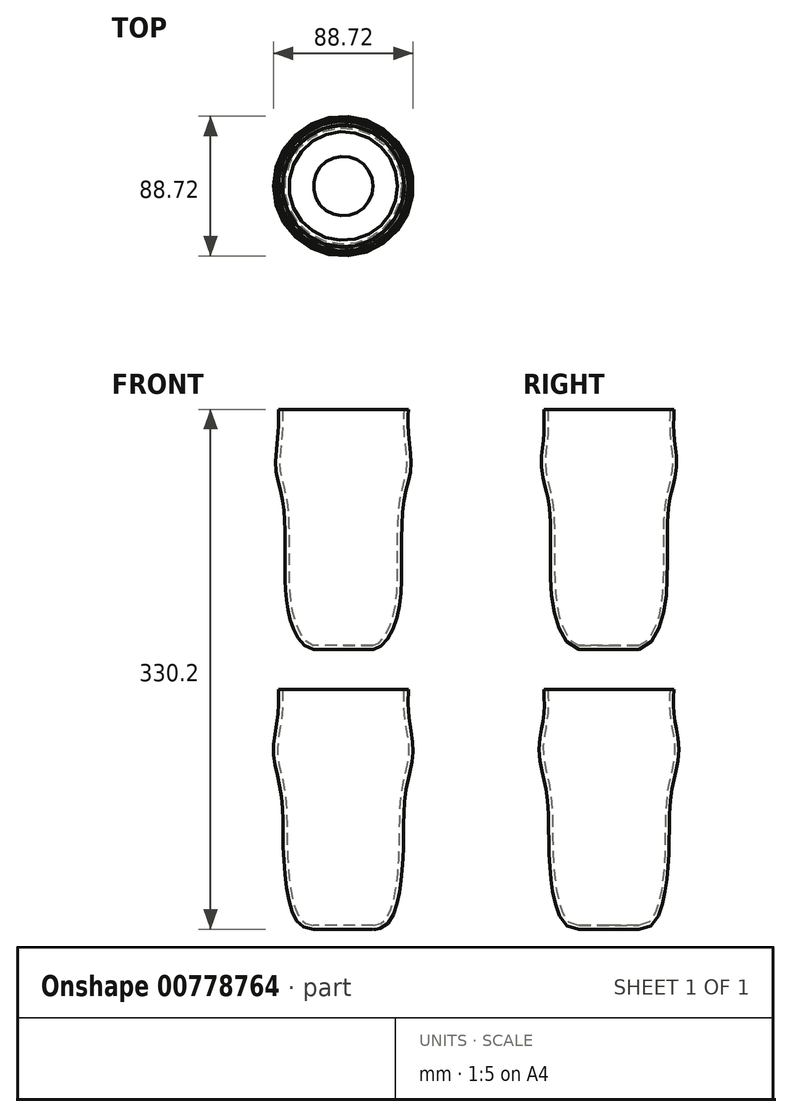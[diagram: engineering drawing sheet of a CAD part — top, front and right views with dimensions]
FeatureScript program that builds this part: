
annotation { "Feature Type Name" : "Feature", "Feature Type Description" : "" }
export const myFeature = defineFeature(function(context is Context, id is Id, definition is map)
    precondition{}
    {
        {
            var Q0;
            Q0=qCreatedBy(makeId("Front.planeOp"),FACE);
            var sketch = newSketch(context, id + "F0", { "sketchPlane" : qUnion([Q0])});
            skLineSegment(sketch, "E0", {"start": v(0, 0) * mm, "end": v(0, 71.05) * mm});
            skLineSegment(sketch, "E1", {"start": v(0, 0) * mm, "end": v(19.05, 0) * mm});
            skFitSpline(sketch, "E2", {"points": [v(19.05, 0) * mm, v(33.3, 13.58) * mm, v(38.15, 53.55) * mm, v(39.83, 88.05) * mm, v(44.35, 113.15) * mm, v(41.28, 137.48) * mm, v(41.28, 152.4) * mm], "startDerivative": vector(169.03, 0) * mm, "endDerivative": vector(0, 63.07) * mm});
            skLineSegment(sketch, "E3", {"start": v(41.28, 152.4) * mm, "end": v(0, 152.4) * mm});
            skLineSegment(sketch, "E4", {"start": v(0, 152.4) * mm, "end": v(0, 71.05) * mm});
            skSolve(sketch);
        }
        {
            var Q0;
            Q0=makeQuery(id+"F0.imprint","IMPRINT",FACE,{"disambiguationData":[TD([[makeQuery(id+"F0.imprint","IMPRINT",EDGE,{"derivedFrom":sQuery(id+"F0.wireOp",EDGE,"E0")}),-1.0]])]});
            var Q1;
            Q1=sQuery(id+"F0.wireOp",EDGE,"E0");
            revolve(context, id + "F1", {"surfaceOperationType" : NewSurfaceOperationType.NEW, "entities" : qUnion([Q0]), "axis" : qUnion([Q1]), "revolveType" : RevolveType.FULL});
        }
        {
            var Q0;
            Q0=makeQuery(id+"F1.opRevolve","SWEPT_FACE",FACE,{"disambiguationData":[OSD([sQuery(id+"F0.wireOp",EDGE,"E3")])]});
            shell(context, id + "F2", {"entities" : qUnion([Q0]), "thickness" : 2.54 * mm});
        }
        {
            var Q0;
            Q0=qCreatedBy(makeId("Front.planeOp"),FACE);
            var sketch = newSketch(context, id + "F3", { "sketchPlane" : qUnion([Q0])});
            skLineSegment(sketch, "E5", {"start": v(0, 177.8) * mm, "end": v(19.05, 177.8) * mm});
            skFitSpline(sketch, "E6", {"points": [v(19.05, 177.8) * mm, v(32.98, 194.5) * mm, v(37.08, 232.59) * mm, v(38.55, 272.43) * mm, v(42.94, 293.52) * mm, v(41.27, 315.28) * mm, v(41.27, 330.2) * mm], "startDerivative": vector(123.55, 11.66) * mm, "endDerivative": vector(0, 63.07) * mm});
            skLineSegment(sketch, "E7", {"start": v(41.27, 330.2) * mm, "end": v(0, 330.2) * mm});
            skLineSegment(sketch, "E8", {"start": v(0, 330.2) * mm, "end": v(0, 177.8) * mm});
            skSolve(sketch);
        }
        {
            var Q0;
            Q0=makeQuery(id+"F3.imprint","IMPRINT",FACE,{"disambiguationData":[TD([[makeQuery(id+"F3.imprint","IMPRINT",EDGE,{"derivedFrom":sQuery(id+"F3.wireOp",EDGE,"E5")}),1.0]])]});
            var Q1;
            Q1=sQuery(id+"F3.wireOp",EDGE,"E8");
            revolve(context, id + "F4", {"surfaceOperationType" : NewSurfaceOperationType.NEW, "entities" : qUnion([Q0]), "axis" : qUnion([Q1]), "revolveType" : RevolveType.FULL});
        }
        {
            var Q0;
            Q0=makeQuery(id+"F4.opRevolve","SWEPT_FACE",FACE,{"disambiguationData":[OSD([sQuery(id+"F3.wireOp",EDGE,"E7")])]});
            shell(context, id + "F5", {"entities" : qUnion([Q0]), "thickness" : 2.54 * mm});
        }
    });
